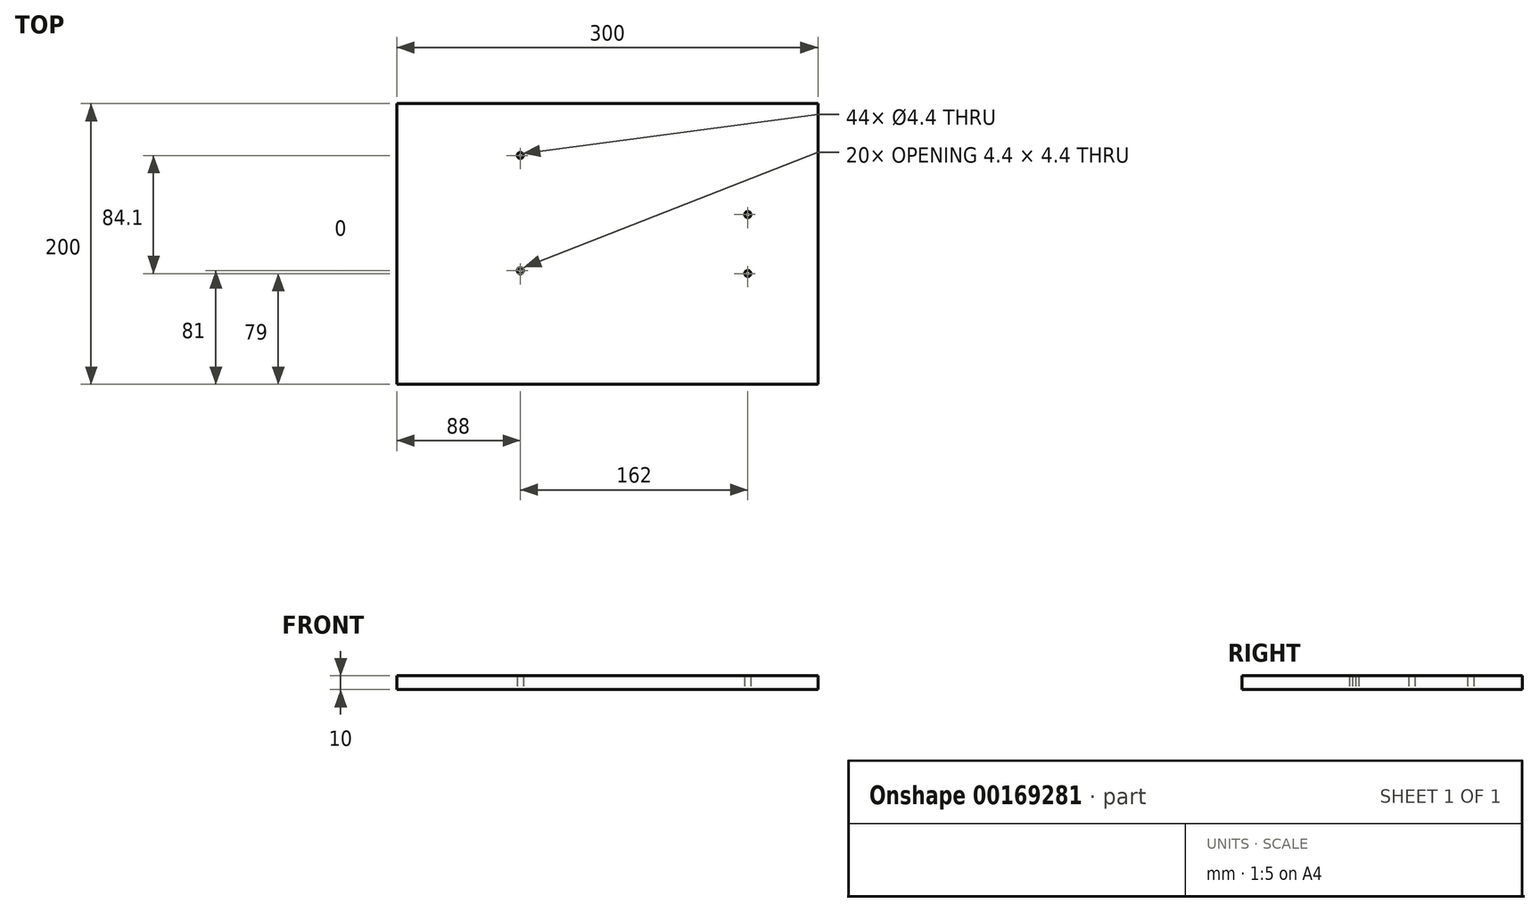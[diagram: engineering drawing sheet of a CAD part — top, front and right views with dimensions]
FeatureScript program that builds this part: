
annotation { "Feature Type Name" : "Feature", "Feature Type Description" : "" }
export const myFeature = defineFeature(function(context is Context, id is Id, definition is map)
    precondition{}
    {
        {
            var Q0;
            Q0=qCreatedBy(makeId("Top.planeOp"),FACE);
            var sketch = newSketch(context, id + "F0", { "sketchPlane" : qUnion([Q0])});
            skLineSegment(sketch, "E0.bottom", {"start": v(0, 0) * mm, "end": v(300, 0) * mm});
            skLineSegment(sketch, "E0.top", {"start": v(0, 200) * mm, "end": v(300, 200) * mm});
            skLineSegment(sketch, "E0.left", {"start": v(0, 0) * mm, "end": v(0, 200) * mm});
            skLineSegment(sketch, "E0.right", {"start": v(300, 0) * mm, "end": v(300, 200) * mm});
            skLineSegment(sketch, "E1", {"start": v(0, 100) * mm, "end": v(300, 100) * mm, "construction": true});
            skLineSegment(sketch, "E2", {"start": v(250, 200) * mm, "end": v(250, 0) * mm, "construction": true});
            skPoint(sketch, "E3", {"position": v(250, 121) * mm});
            skPoint(sketch, "E4", {"position": v(250, 79) * mm});
            skLineSegment(sketch, "E5", {"start": v(88, 200) * mm, "end": v(88, 0) * mm, "construction": true});
            skPoint(sketch, "E6", {"position": v(88, 163.1) * mm});
            skPoint(sketch, "E7", {"position": v(88, 81) * mm});
            skSolve(sketch);
        }
        {
            var Q0;
            Q0 = qSketchRegion(id + "F0", true);
            extrude(context, id + "F1", {"entities" : qUnion([Q0]), "depth" : 10 * mm});
        }
        {
            var Q0;
            Q0=sQuery(id+"F0.wireOp",VERTEX,"E3");
            var Q1;
            Q1=sQuery(id+"F0.wireOp",VERTEX,"E4");
            var Q2;
            Q2=sQuery(id+"F0.wireOp",VERTEX,"E7");
            var Q3;
            Q3=sQuery(id+"F0.wireOp",VERTEX,"E6");
            var Q4;
            Q4=makeQuery(id+"F1.opExtrude","SWEPT_BODY",BODY,{"disambiguationData":[OSD([sQuery(id+"F0.wireOp",EDGE,"E0.bottom"),sQuery(id+"F0.wireOp",EDGE,"E0.top"),sQuery(id+"F0.wireOp",EDGE,"E0.left"),sQuery(id+"F0.wireOp",EDGE,"E0.right")])]});
            hole(context, id + "F2", {"style" : HoleStyle.SIMPLE, "endStyle" : HoleEndStyle.THROUGH, "oppositeDirection" : true, "standardTappedOrClearance" : lookupTablePath({ "standard" : "ISO", "fit" : "Normal", "size" : "M4", "type" : "Clearance" }), "standardBlindInLast" : lookupTablePath({ "fit" : "Standard", "standard" : "ISO", "size" : "M4", "type" : "Clearance" }), "holeDiameter" : 4.4 * mm, "locations" : qUnion([Q0, Q1, Q2, Q3]), "scope" : qUnion([Q4]), "isTappedThrough" : true});
        }
    });
